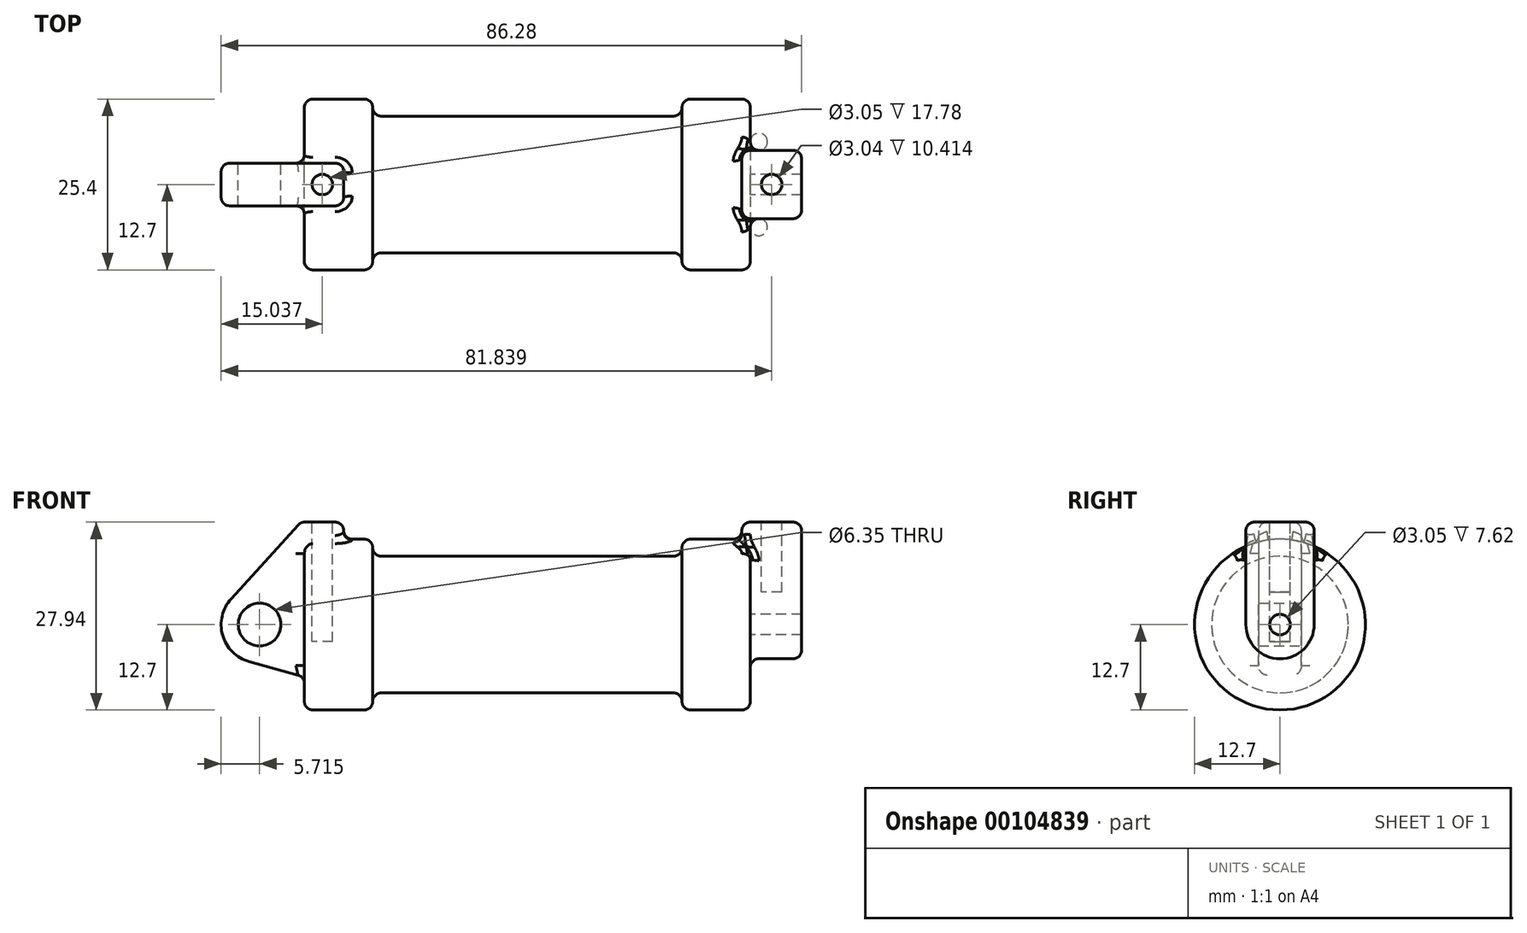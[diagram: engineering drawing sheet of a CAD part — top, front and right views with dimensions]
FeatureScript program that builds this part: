
annotation { "Feature Type Name" : "Feature", "Feature Type Description" : "" }
export const myFeature = defineFeature(function(context is Context, id is Id, definition is map)
    precondition{}
    {
        {
            var Q0;
            Q0=qCreatedBy(makeId("Front.planeOp"),FACE);
            var sketch = newSketch(context, id + "F0", { "sketchPlane" : qUnion([Q0])});
            skLineSegment(sketch, "E0", {"start": v(0, 0) * mm, "end": v(0, 12.7) * mm});
            skLineSegment(sketch, "E1", {"start": v(0, 12.7) * mm, "end": v(10.16, 12.7) * mm});
            skLineSegment(sketch, "E2", {"start": v(10.16, 12.7) * mm, "end": v(10.16, 10.16) * mm});
            skLineSegment(sketch, "E3", {"start": v(10.16, 10.16) * mm, "end": v(56.13, 10.16) * mm});
            skLineSegment(sketch, "E4", {"start": v(56.13, 10.16) * mm, "end": v(56.13, 12.7) * mm});
            skLineSegment(sketch, "E5", {"start": v(56.13, 12.7) * mm, "end": v(66.3, 12.7) * mm});
            skLineSegment(sketch, "E6", {"start": v(66.3, 12.7) * mm, "end": v(66.3, 0) * mm});
            skLineSegment(sketch, "E7", {"start": v(66.3, 0) * mm, "end": v(0, 0) * mm});
            skLineSegment(sketch, "E8", {"start": v(5.84, 15.24) * mm, "end": v(-0.5, 15.24) * mm});
            skLineSegment(sketch, "E9", {"start": v(-0.5, 15.24) * mm, "end": v(-10.88, 3.85) * mm});
            skLineSegment(sketch, "E10", {"start": v(0, 0) * mm, "end": v(-6.65, 0) * mm});
            skCircle(sketch, "E11", {"center": v(-6.65, 0) * mm, "radius": 5.72 * mm});
            skCircle(sketch, "E12", {"center": v(-6.65, 0) * mm, "radius": 3.18 * mm});
            skLineSegment(sketch, "E13", {"start": v(5.84, 15.24) * mm, "end": v(5.84, -9.4) * mm});
            skLineSegment(sketch, "E14", {"start": v(5.84, -9.4) * mm, "end": v(-8.18, -5.5) * mm});
            skSolve(sketch);
        }
        {
            var Q0;
            {var subQ0=sQuery(id+"F0.wireOp",EDGE,"E2");Q0=makeQuery(id+"F0.imprint","IMPRINT",FACE,{"disambiguationData":[TD([[makeQuery(id+"F0.imprint","IMPRINT",EDGE,{"derivedFrom":subQ0}),-1.0]])]});}
            var Q1;
            {var subQ0=sQuery(id+"F0.wireOp",EDGE,"E0");Q1=makeQuery(id+"F0.imprint","IMPRINT",FACE,{"disambiguationData":[TD([[makeQuery(id+"F0.imprint","IMPRINT",EDGE,{"derivedFrom":subQ0}),-1.0]])]});}
            var Q2;
            Q2=sQuery(id+"F0.wireOp",EDGE,"E7");
            revolve(context, id + "F1", {"entities" : qUnion([Q0, Q1]), "axis" : qUnion([Q2]), "revolveType" : RevolveType.FULL});
        }
        {
            var Q0;
            {var subQ0=sQuery(id+"F0.wireOp",EDGE,"E0");Q0=makeQuery(id+"F0.imprint","IMPRINT",FACE,{"disambiguationData":[TD([[makeQuery(id+"F0.imprint","IMPRINT",EDGE,{"derivedFrom":subQ0}),-1.0]])]});}
            var Q1;
            {var subQ3=sQuery(id+"F0.wireOp",EDGE,"E0");Q1=makeQuery(id+"F0.imprint","IMPRINT",FACE,{"disambiguationData":[TD([[makeQuery(id+"F0.imprint","IMPRINT",EDGE,{"derivedFrom":subQ3}),1.0]])]});}
            var Q2;
            {var subQ0=sQuery(id+"F0.wireOp",EDGE,"E14");Q2=makeQuery(id+"F0.imprint","IMPRINT",FACE,{"disambiguationData":[TD([[makeQuery(id+"F0.imprint","IMPRINT",EDGE,{"derivedFrom":subQ0}),-1.0]])]});}
            var Q3;
            {var subQ4=sQuery(id+"F0.wireOp",EDGE,"E12");Q3=makeQuery(id+"F0.imprint","IMPRINT",FACE,{"disambiguationData":[TD([[makeQuery(id+"F0.imprint","IMPRINT",EDGE,{"derivedFrom":subQ4}),-1.0]])]});}
            extrude(context, id + "F2", {"entities" : qUnion([Q0, Q1, Q2, Q3]), "operationType" : NewBodyOperationType.ADD, "endBound" : BoundingType.SYMMETRIC, "depth" : 6.35 * mm});
        }
        {
            var Q0;
            Q0=makeQuery(id+"F1.opRevolve","SWEPT_FACE",FACE,{"disambiguationData":[OSD([sQuery(id+"F0.wireOp",EDGE,"E6")])]});
            var sketch = newSketch(context, id + "F3", { "sketchPlane" : qUnion([Q0])});
            skCircle(sketch, "E15", {"center": v(0, 0) * mm, "radius": 1.52 * mm});
            skCircle(sketch, "E16", {"center": v(0, 0) * mm, "radius": 5.08 * mm});
            skLineSegment(sketch, "E17", {"start": v(5.08, 0) * mm, "end": v(5.08, 15.24) * mm});
            skLineSegment(sketch, "E18", {"start": v(-5.08, 0) * mm, "end": v(-5.08, 15.24) * mm});
            skLineSegment(sketch, "E19", {"start": v(-5.08, 15.24) * mm, "end": v(5.08, 15.24) * mm});
            skSolve(sketch);
        }
        {
            var Q0;
            {var subQ0=sQuery(id+"F3.wireOp",EDGE,"E19");Q0=makeQuery(id+"F3.imprint","IMPRINT",FACE,{"disambiguationData":[TD([[makeQuery(id+"F3.imprint","IMPRINT",EDGE,{"derivedFrom":subQ0}),-1.0]])]});}
            var Q1;
            {var subQ0=sQuery(id+"F3.wireOp",EDGE,"E17");var subQ1=sQuery(id+"F3.wireOp",EDGE,"E16");var subQ2=makeQuery(id+"F3.imprint","INTERSECT",VERTEX,{"derivedFrom":[subQ1,subQ0]});Q1=makeQuery(id+"F3.imprint","IMPRINT",FACE,{"disambiguationData":[TD([[makeQuery(id+"F3.imprint","IMPRINT",EDGE,{"disambiguationData":[TD([[subQ2,-1.0]])],"derivedFrom":subQ1}),-1.0]])]});}
            var Q2;
            Q2=makeQuery(id+"F3.imprint","IMPRINT",FACE,{"disambiguationData":[TD([[makeQuery(id+"F3.imprint","IMPRINT",EDGE,{"derivedFrom":sQuery(id+"F3.wireOp",EDGE,"E15")}),-1.0]])]});
            extrude(context, id + "F4", {"entities" : qUnion([Q0, Q1, Q2]), "operationType" : NewBodyOperationType.ADD, "depth" : 7.62 * mm, "hasSecondDirection" : true, "secondDirectionOppositeDirection" : true, "secondDirectionDepth" : 1.27 * mm});
        }
        {
            var Q0;
            Q0=makeQuery(id+"F4.opExtrude","SWEPT_FACE",FACE,{"disambiguationData":[OSD([sQuery(id+"F3.wireOp",EDGE,"E19")])]});
            var sketch = newSketch(context, id + "F5", { "sketchPlane" : qUnion([Q0])});
            skCircle(sketch, "E20", {"center": v(69.47, 0) * mm, "radius": 1.52 * mm});
            skPoint(sketch, "E20.centerSnap0", {"position": v(65.02, 0) * mm});
            skPoint(sketch, "E20.centerSnap1", {"position": v(69.47, 5.08) * mm});
            skSolve(sketch);
        }
        {
            var Q0;
            Q0=makeQuery(id+"F2.opExtrude","SWEPT_FACE",FACE,{"disambiguationData":[OSD([sQuery(id+"F0.wireOp",EDGE,"E8")])]});
            var sketch = newSketch(context, id + "F6", { "sketchPlane" : qUnion([Q0])});
            skCircle(sketch, "E21", {"center": v(2.67, 0) * mm, "radius": 1.52 * mm});
            skPoint(sketch, "E21.centerSnap0", {"position": v(5.84, 0) * mm});
            skPoint(sketch, "E21.centerSnap1", {"position": v(2.67, 3.18) * mm});
            skSolve(sketch);
        }
        {
            var Q0;
            Q0=makeQuery(id+"F6.imprint","IMPRINT",FACE,{"disambiguationData":[TD([[makeQuery(id+"F6.imprint","IMPRINT",EDGE,{"derivedFrom":sQuery(id+"F6.wireOp",EDGE,"E21")}),1.0]])]});
            extrude(context, id + "F7", {"entities" : qUnion([Q0]), "operationType" : NewBodyOperationType.REMOVE, "oppositeDirection" : true, "depth" : 17.78 * mm});
        }
        {
            var Q0;
            Q0=makeQuery(id+"F5.imprint","IMPRINT",FACE,{"disambiguationData":[TD([[makeQuery(id+"F5.imprint","IMPRINT",EDGE,{"derivedFrom":sQuery(id+"F5.wireOp",EDGE,"E20")}),1.0]])]});
            extrude(context, id + "F8", {"entities" : qUnion([Q0]), "operationType" : NewBodyOperationType.REMOVE, "oppositeDirection" : true, "depth" : 10.4 * mm});
        }
        {
            var Q0;
            Q0=makeQuery(id+"F1.opRevolve","SWEPT_EDGE",EDGE,{"disambiguationData":[OSD([sQuery(id+"F0.wireOp",EDGE,"E2"),sQuery(id+"F0.wireOp",EDGE,"E3")])]});
            var Q1;
            Q1=makeQuery(id+"F1.opRevolve","SWEPT_EDGE",EDGE,{"disambiguationData":[OSD([sQuery(id+"F0.wireOp",EDGE,"E1"),sQuery(id+"F0.wireOp",EDGE,"E2")])]});
            var Q2;
            Q2=makeQuery(id+"F1.opRevolve","SWEPT_EDGE",EDGE,{"disambiguationData":[OSD([sQuery(id+"F0.wireOp",EDGE,"E0"),sQuery(id+"F0.wireOp",EDGE,"E1")])]});
            var Q3;
            Q3=makeQuery(id+"F2.boolean.opBoolean","INTERSECT",EDGE,{"derivedFrom":[makeQuery(id+"F1.opRevolve","SWEPT_FACE",FACE,{"disambiguationData":[OSD([sQuery(id+"F0.wireOp",EDGE,"E1")])]}),makeQuery(id+"F2.opExtrude","CAP_FACE",FACE,{"disambiguationData":[OSD([sQuery(id+"F0.wireOp",EDGE,"E8"),sQuery(id+"F0.wireOp",EDGE,"E9"),sQuery(id+"F0.wireOp",EDGE,"E11"),sQuery(id+"F0.wireOp",EDGE,"E12"),sQuery(id+"F0.wireOp",EDGE,"E13"),sQuery(id+"F0.wireOp",EDGE,"E14")])],"isStart":false})]});
            var Q4;
            Q4=makeQuery(id+"F2.boolean.opBoolean","INTERSECT",EDGE,{"derivedFrom":[makeQuery(id+"F1.opRevolve","SWEPT_FACE",FACE,{"disambiguationData":[OSD([sQuery(id+"F0.wireOp",EDGE,"E1")])]}),makeQuery(id+"F2.opExtrude","SWEPT_FACE",FACE,{"disambiguationData":[OSD([sQuery(id+"F0.wireOp",EDGE,"E13")])]})]});
            var Q5;
            Q5=makeQuery(id+"F2.boolean.opBoolean","INTERSECT",EDGE,{"derivedFrom":[makeQuery(id+"F1.opRevolve","SWEPT_FACE",FACE,{"disambiguationData":[OSD([sQuery(id+"F0.wireOp",EDGE,"E1")])]}),makeQuery(id+"F2.opExtrude","CAP_FACE",FACE,{"disambiguationData":[OSD([sQuery(id+"F0.wireOp",EDGE,"E8"),sQuery(id+"F0.wireOp",EDGE,"E9"),sQuery(id+"F0.wireOp",EDGE,"E11"),sQuery(id+"F0.wireOp",EDGE,"E12"),sQuery(id+"F0.wireOp",EDGE,"E13"),sQuery(id+"F0.wireOp",EDGE,"E14")])],"isStart":true})]});
            var Q6;
            Q6=makeQuery(id+"F2.opExtrude","CAP_EDGE",EDGE,{"disambiguationData":[OSD([sQuery(id+"F0.wireOp",EDGE,"E8")])],"isStart":true});
            var Q7;
            Q7=makeQuery(id+"F2.opExtrude","SWEPT_EDGE",EDGE,{"disambiguationData":[OSD([sQuery(id+"F0.wireOp",EDGE,"E8"),sQuery(id+"F0.wireOp",EDGE,"E13")])]});
            var Q8;
            Q8=makeQuery(id+"F2.opExtrude","CAP_EDGE",EDGE,{"disambiguationData":[OSD([sQuery(id+"F0.wireOp",EDGE,"E9")])],"isStart":false});
            var Q9;
            Q9=makeQuery(id+"F2.opExtrude","CAP_EDGE",EDGE,{"disambiguationData":[OSD([sQuery(id+"F0.wireOp",EDGE,"E8")])],"isStart":false});
            var Q10;
            Q10=makeQuery(id+"F2.opExtrude","SWEPT_EDGE",EDGE,{"disambiguationData":[OSD([sQuery(id+"F0.wireOp",EDGE,"E8"),sQuery(id+"F0.wireOp",EDGE,"E9")])]});
            var Q11;
            Q11=makeQuery(id+"F2.opExtrude","CAP_EDGE",EDGE,{"disambiguationData":[OSD([sQuery(id+"F0.wireOp",EDGE,"E9")])],"isStart":true});
            var Q12;
            Q12=makeQuery(id+"F2.opExtrude","CAP_EDGE",EDGE,{"disambiguationData":[OSD([sQuery(id+"F0.wireOp",EDGE,"E13")])],"isStart":false});
            var Q13;
            Q13=makeQuery(id+"F2.opExtrude","CAP_EDGE",EDGE,{"disambiguationData":[OSD([sQuery(id+"F0.wireOp",EDGE,"E13")])],"isStart":true});
            var Q14;
            Q14=makeQuery(id+"F2.opExtrude","SWEPT_EDGE",EDGE,{"disambiguationData":[OSD([sQuery(id+"F0.wireOp",EDGE,"E9"),sQuery(id+"F0.wireOp",EDGE,"E11")])]});
            var Q15;
            Q15=makeQuery(id+"F2.opExtrude","CAP_EDGE",EDGE,{"disambiguationData":[OSD([sQuery(id+"F0.wireOp",EDGE,"E11")])],"isStart":false});
            var Q16;
            Q16=makeQuery(id+"F2.opExtrude","CAP_EDGE",EDGE,{"disambiguationData":[OSD([sQuery(id+"F0.wireOp",EDGE,"E11")])],"isStart":true});
            var Q17;
            Q17=makeQuery(id+"F2.opExtrude","SWEPT_EDGE",EDGE,{"disambiguationData":[OSD([sQuery(id+"F0.wireOp",EDGE,"E11"),sQuery(id+"F0.wireOp",EDGE,"E14")])]});
            var Q18;
            Q18=makeQuery(id+"F2.boolean.opBoolean","INTERSECT",EDGE,{"derivedFrom":[makeQuery(id+"F1.opRevolve","SWEPT_FACE",FACE,{"disambiguationData":[OSD([sQuery(id+"F0.wireOp",EDGE,"E0")])]}),makeQuery(id+"F2.opExtrude","SWEPT_FACE",FACE,{"disambiguationData":[OSD([sQuery(id+"F0.wireOp",EDGE,"E14")])]})]});
            var Q19;
            Q19=makeQuery(id+"F2.opExtrude","CAP_EDGE",EDGE,{"disambiguationData":[OSD([sQuery(id+"F0.wireOp",EDGE,"E14")])],"isStart":false});
            var Q20;
            Q20=makeQuery(id+"F2.boolean.opBoolean","INTERSECT",EDGE,{"derivedFrom":[makeQuery(id+"F1.opRevolve","SWEPT_FACE",FACE,{"disambiguationData":[OSD([sQuery(id+"F0.wireOp",EDGE,"E0")])]}),makeQuery(id+"F2.opExtrude","CAP_FACE",FACE,{"disambiguationData":[OSD([sQuery(id+"F0.wireOp",EDGE,"E8"),sQuery(id+"F0.wireOp",EDGE,"E9"),sQuery(id+"F0.wireOp",EDGE,"E11"),sQuery(id+"F0.wireOp",EDGE,"E12"),sQuery(id+"F0.wireOp",EDGE,"E13"),sQuery(id+"F0.wireOp",EDGE,"E14")])],"isStart":true})]});
            var Q21;
            Q21=makeQuery(id+"F2.opExtrude","CAP_EDGE",EDGE,{"disambiguationData":[OSD([sQuery(id+"F0.wireOp",EDGE,"E14")])],"isStart":true});
            var Q22;
            Q22=makeQuery(id+"F2.boolean.opBoolean","INTERSECT",EDGE,{"derivedFrom":[makeQuery(id+"F1.opRevolve","SWEPT_FACE",FACE,{"disambiguationData":[OSD([sQuery(id+"F0.wireOp",EDGE,"E0")])]}),makeQuery(id+"F2.opExtrude","CAP_FACE",FACE,{"disambiguationData":[OSD([sQuery(id+"F0.wireOp",EDGE,"E8"),sQuery(id+"F0.wireOp",EDGE,"E9"),sQuery(id+"F0.wireOp",EDGE,"E11"),sQuery(id+"F0.wireOp",EDGE,"E12"),sQuery(id+"F0.wireOp",EDGE,"E13"),sQuery(id+"F0.wireOp",EDGE,"E14")])],"isStart":false})]});
            var Q23;
            Q23=makeQuery(id+"F4.opExtrude","CAP_EDGE",EDGE,{"disambiguationData":[OSD([sQuery(id+"F3.wireOp",EDGE,"E17")])],"isStart":false});
            var Q24;
            Q24=makeQuery(id+"F4.opExtrude","CAP_EDGE",EDGE,{"disambiguationData":[OSD([sQuery(id+"F3.wireOp",EDGE,"E18")])],"isStart":false});
            var Q25;
            Q25=makeQuery(id+"F4.opExtrude","CAP_EDGE",EDGE,{"disambiguationData":[OSD([sQuery(id+"F3.wireOp",EDGE,"E19")])],"isStart":false});
            var Q26;
            Q26=makeQuery(id+"F4.opExtrude","CAP_EDGE",EDGE,{"disambiguationData":[OSD([sQuery(id+"F3.wireOp",EDGE,"E16")])],"isStart":false});
            var Q27;
            Q27=makeQuery(id+"F4.opExtrude","SWEPT_EDGE",EDGE,{"disambiguationData":[OSD([sQuery(id+"F3.wireOp",EDGE,"E16"),sQuery(id+"F3.wireOp",EDGE,"E17")])]});
            var Q28;
            Q28=makeQuery(id+"F4.boolean.opBoolean","INTERSECT",EDGE,{"derivedFrom":[makeQuery(id+"F1.opRevolve","SWEPT_FACE",FACE,{"disambiguationData":[OSD([sQuery(id+"F0.wireOp",EDGE,"E6")])]}),makeQuery(id+"F4.opExtrude","SWEPT_FACE",FACE,{"disambiguationData":[OSD([sQuery(id+"F3.wireOp",EDGE,"E17")])]})]});
            var Q29;
            Q29=makeQuery(id+"F4.boolean.opBoolean","INTERSECT",EDGE,{"derivedFrom":[makeQuery(id+"F1.opRevolve","SWEPT_FACE",FACE,{"disambiguationData":[OSD([sQuery(id+"F0.wireOp",EDGE,"E5")])]}),makeQuery(id+"F4.opExtrude","SWEPT_FACE",FACE,{"disambiguationData":[OSD([sQuery(id+"F3.wireOp",EDGE,"E17")])]})]});
            var Q30;
            Q30=makeQuery(id+"F4.opExtrude","CAP_EDGE",EDGE,{"disambiguationData":[OSD([sQuery(id+"F3.wireOp",EDGE,"E17")])],"isStart":true});
            var Q31;
            Q31=makeQuery(id+"F4.opExtrude","SWEPT_EDGE",EDGE,{"disambiguationData":[OSD([sQuery(id+"F3.wireOp",EDGE,"E17"),sQuery(id+"F3.wireOp",EDGE,"E19")])]});
            var Q32;
            Q32=makeQuery(id+"F4.opExtrude","SWEPT_EDGE",EDGE,{"disambiguationData":[OSD([sQuery(id+"F3.wireOp",EDGE,"E18"),sQuery(id+"F3.wireOp",EDGE,"E19")])]});
            var Q33;
            Q33=makeQuery(id+"F4.opExtrude","CAP_EDGE",EDGE,{"disambiguationData":[OSD([sQuery(id+"F3.wireOp",EDGE,"E19")])],"isStart":true});
            var Q34;
            Q34=makeQuery(id+"F4.boolean.opBoolean","INTERSECT",EDGE,{"derivedFrom":[makeQuery(id+"F1.opRevolve","SWEPT_FACE",FACE,{"disambiguationData":[OSD([sQuery(id+"F0.wireOp",EDGE,"E5")])]}),makeQuery(id+"F4.opExtrude","CAP_FACE",FACE,{"disambiguationData":[OSD([sQuery(id+"F3.wireOp",EDGE,"E15"),sQuery(id+"F3.wireOp",EDGE,"E16"),sQuery(id+"F3.wireOp",EDGE,"E17"),sQuery(id+"F3.wireOp",EDGE,"E18"),sQuery(id+"F3.wireOp",EDGE,"E19")])],"isStart":true})]});
            var Q35;
            Q35=makeQuery(id+"F4.opExtrude","CAP_EDGE",EDGE,{"disambiguationData":[OSD([sQuery(id+"F3.wireOp",EDGE,"E18")])],"isStart":true});
            var Q36;
            Q36=makeQuery(id+"F4.boolean.opBoolean","INTERSECT",EDGE,{"derivedFrom":[makeQuery(id+"F1.opRevolve","SWEPT_FACE",FACE,{"disambiguationData":[OSD([sQuery(id+"F0.wireOp",EDGE,"E5")])]}),makeQuery(id+"F4.opExtrude","SWEPT_FACE",FACE,{"disambiguationData":[OSD([sQuery(id+"F3.wireOp",EDGE,"E18")])]})]});
            var Q37;
            Q37=makeQuery(id+"F1.opRevolve","SWEPT_EDGE",EDGE,{"disambiguationData":[OSD([sQuery(id+"F0.wireOp",EDGE,"E3"),sQuery(id+"F0.wireOp",EDGE,"E4")])]});
            var Q38;
            Q38=makeQuery(id+"F1.opRevolve","SWEPT_EDGE",EDGE,{"disambiguationData":[OSD([sQuery(id+"F0.wireOp",EDGE,"E4"),sQuery(id+"F0.wireOp",EDGE,"E5")])]});
            var Q39;
            Q39=makeQuery(id+"F4.opExtrude","SWEPT_EDGE",EDGE,{"disambiguationData":[OSD([sQuery(id+"F3.wireOp",EDGE,"E16"),sQuery(id+"F3.wireOp",EDGE,"E18")])]});
            var Q40;
            Q40=makeQuery(id+"F4.boolean.opBoolean","INTERSECT",EDGE,{"derivedFrom":[makeQuery(id+"F1.opRevolve","SWEPT_FACE",FACE,{"disambiguationData":[OSD([sQuery(id+"F0.wireOp",EDGE,"E6")])]}),makeQuery(id+"F4.opExtrude","SWEPT_FACE",FACE,{"disambiguationData":[OSD([sQuery(id+"F3.wireOp",EDGE,"E18")])]})]});
            var Q41;
            Q41=makeQuery(id+"F4.boolean.opBoolean","INTERSECT",EDGE,{"derivedFrom":[makeQuery(id+"F1.opRevolve","SWEPT_FACE",FACE,{"disambiguationData":[OSD([sQuery(id+"F0.wireOp",EDGE,"E6")])]}),makeQuery(id+"F4.opExtrude","SWEPT_FACE",FACE,{"disambiguationData":[OSD([sQuery(id+"F3.wireOp",EDGE,"E16")])]})]});
            var Q42;
            Q42=makeQuery(id+"F1.opRevolve","SWEPT_EDGE",EDGE,{"disambiguationData":[OSD([sQuery(id+"F0.wireOp",EDGE,"E5"),sQuery(id+"F0.wireOp",EDGE,"E6")])]});
            fillet(context, id + "F9", {"entities" : qUnion([Q0, Q1, Q2, Q3, Q4, Q5, Q6, Q7, Q8, Q9, Q10, Q11, Q12, Q13, Q14, Q15, Q16, Q17, Q18, Q19, Q20, Q21, Q22, Q23, Q24, Q25, Q26, Q27, Q28, Q29, Q30, Q31, Q32, Q33, Q34, Q35, Q36, Q37, Q38, Q39, Q40, Q41, Q42]), "radius" : 1.27 * mm, "tangentPropagation" : true, "allowEdgeOverflow" : false});
        }
    });
